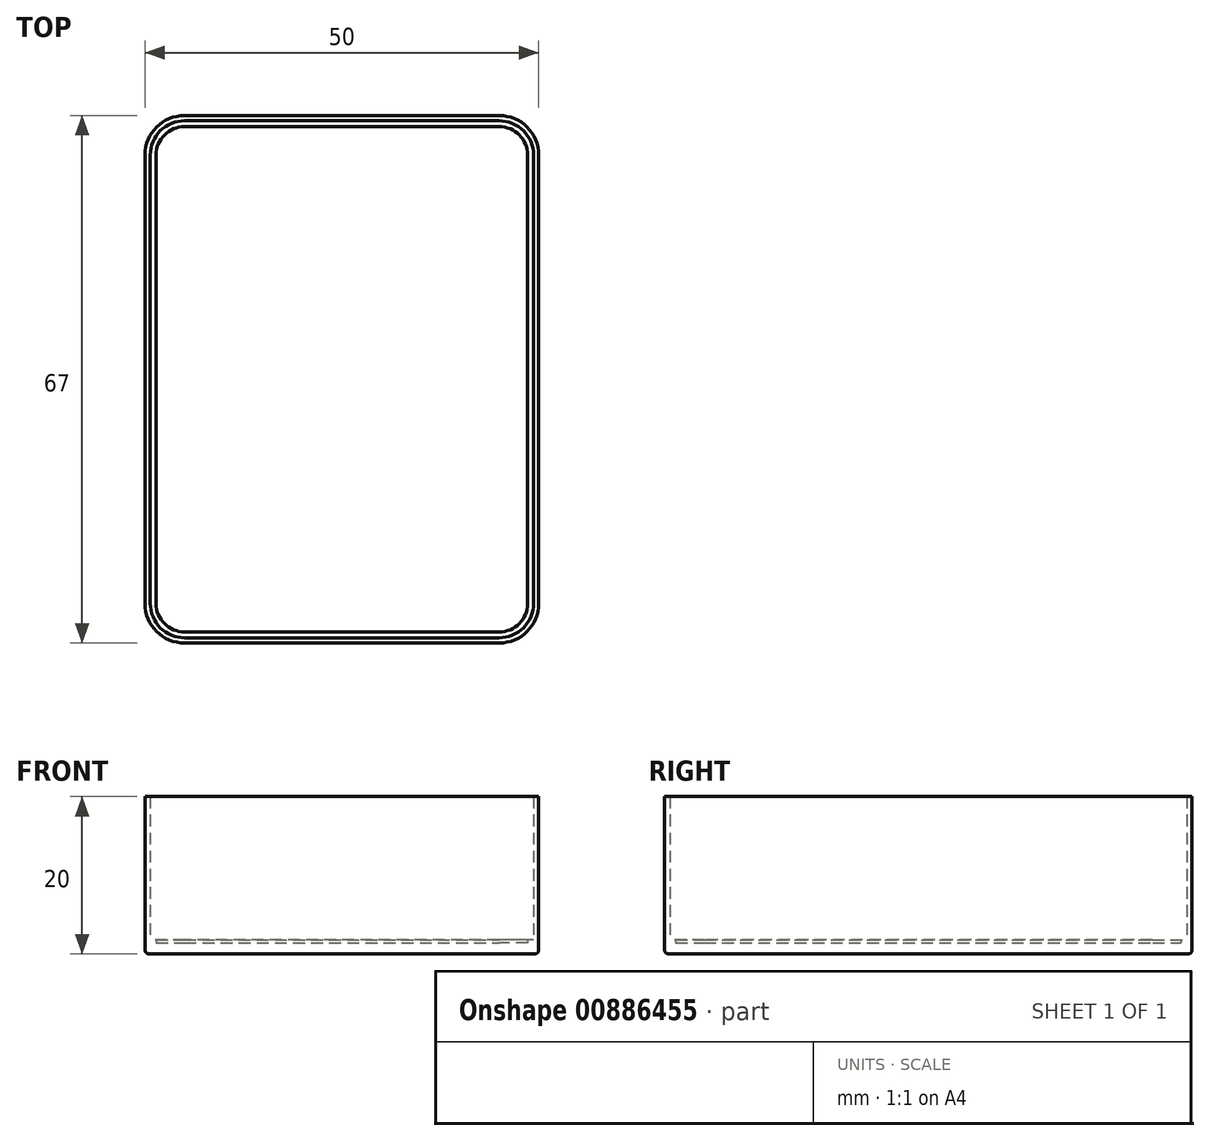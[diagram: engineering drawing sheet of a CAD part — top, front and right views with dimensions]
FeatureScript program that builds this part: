
annotation { "Feature Type Name" : "Feature", "Feature Type Description" : "" }
export const myFeature = defineFeature(function(context is Context, id is Id, definition is map)
    precondition{}
    {
        {
            assignVariable(context, id + "F0", {"name" : "Wandstaerke", "anyValue" : 1.4});
        }
        {
            assignVariable(context, id + "F1", {"name" : "Boxhoehe", "anyValue" : 20});
        }
        {
            assignVariable(context, id + "F2", {"name" : "Abrundungen", "anyValue" : 0.5});
        }
        {
            var Q0;
            Q0=qCreatedBy(makeId("Top.planeOp"),FACE);
            var sketch = newSketch(context, id + "F3", { "sketchPlane" : qUnion([Q0])});
            skLineSegment(sketch, "E0.bottom", {"start": v(-20, -33.5) * mm, "end": v(20, -33.5) * mm});
            skLineSegment(sketch, "E0.top", {"start": v(-20, 33.5) * mm, "end": v(20, 33.5) * mm});
            skLineSegment(sketch, "E0.left", {"start": v(-25, -28.5) * mm, "end": v(-25, 28.5) * mm});
            skLineSegment(sketch, "E0.right", {"start": v(25, -28.5) * mm, "end": v(25, 28.5) * mm});
            skPoint(sketch, "E0.middle", {"position": v(0, 0) * mm});
            skLineSegment(sketch, "E1.bottom", {"start": v(-20, -32.1) * mm, "end": v(20, -32.1) * mm});
            skLineSegment(sketch, "E1.top", {"start": v(-20, 32.1) * mm, "end": v(20, 32.1) * mm});
            skLineSegment(sketch, "E1.left", {"start": v(-23.6, -28.5) * mm, "end": v(-23.6, 28.5) * mm});
            skLineSegment(sketch, "E1.right", {"start": v(23.6, -28.5) * mm, "end": v(23.6, 28.5) * mm});
            skLineSegment(sketch, "E2.bottom", {"start": v(19.95, 32.85) * mm, "end": v(-19.95, 32.85) * mm});
            skLineSegment(sketch, "E2.top", {"start": v(19.95, -32.85) * mm, "end": v(-19.95, -32.85) * mm});
            skLineSegment(sketch, "E2.left", {"start": v(24.35, 28.45) * mm, "end": v(24.35, -28.45) * mm});
            skLineSegment(sketch, "E2.right", {"start": v(-24.35, 28.45) * mm, "end": v(-24.35, -28.45) * mm});
            skPoint(sketch, "E3.visualSharp", {"position": v(23.6, -32.1) * mm});
            skArc(sketch, "E3.filletArc", {"start": v(20, -32.1) * mm, "mid": v(22.55, -31.05) * mm, "end": v(23.6, -28.5) * mm});
            skPoint(sketch, "E4.visualSharp", {"position": v(24.35, -32.85) * mm});
            skArc(sketch, "E4.filletArc", {"start": v(19.95, -32.85) * mm, "mid": v(23.06, -31.56) * mm, "end": v(24.35, -28.45) * mm});
            skPoint(sketch, "E5.visualSharp", {"position": v(25, -33.5) * mm});
            skArc(sketch, "E5.filletArc", {"start": v(20, -33.5) * mm, "mid": v(23.54, -32.04) * mm, "end": v(25, -28.5) * mm});
            skPoint(sketch, "E6.visualSharp", {"position": v(23.6, 32.1) * mm});
            skArc(sketch, "E6.filletArc", {"start": v(23.6, 28.5) * mm, "mid": v(22.55, 31.05) * mm, "end": v(20, 32.1) * mm});
            skPoint(sketch, "E7.visualSharp", {"position": v(24.35, 32.85) * mm});
            skArc(sketch, "E7.filletArc", {"start": v(24.35, 28.45) * mm, "mid": v(23.06, 31.56) * mm, "end": v(19.95, 32.85) * mm});
            skPoint(sketch, "E8.visualSharp", {"position": v(25, 33.5) * mm});
            skArc(sketch, "E8.filletArc", {"start": v(25, 28.5) * mm, "mid": v(23.54, 32.04) * mm, "end": v(20, 33.5) * mm});
            skPoint(sketch, "E9.visualSharp", {"position": v(-23.6, 32.1) * mm});
            skArc(sketch, "E9.filletArc", {"start": v(-20, 32.1) * mm, "mid": v(-22.55, 31.05) * mm, "end": v(-23.6, 28.5) * mm});
            skPoint(sketch, "E10.visualSharp", {"position": v(-24.35, 32.85) * mm});
            skArc(sketch, "E10.filletArc", {"start": v(-19.95, 32.85) * mm, "mid": v(-23.06, 31.56) * mm, "end": v(-24.35, 28.45) * mm});
            skPoint(sketch, "E11.visualSharp", {"position": v(-25, 33.5) * mm});
            skArc(sketch, "E11.filletArc", {"start": v(-20, 33.5) * mm, "mid": v(-23.54, 32.04) * mm, "end": v(-25, 28.5) * mm});
            skPoint(sketch, "E12.visualSharp", {"position": v(-23.6, -32.1) * mm});
            skArc(sketch, "E12.filletArc", {"start": v(-23.6, -28.5) * mm, "mid": v(-22.55, -31.05) * mm, "end": v(-20, -32.1) * mm});
            skPoint(sketch, "E13.visualSharp", {"position": v(-24.35, -32.85) * mm});
            skArc(sketch, "E13.filletArc", {"start": v(-24.35, -28.45) * mm, "mid": v(-23.06, -31.56) * mm, "end": v(-19.95, -32.85) * mm});
            skPoint(sketch, "E14.visualSharp", {"position": v(-25, -33.5) * mm});
            skArc(sketch, "E14.filletArc", {"start": v(-25, -28.5) * mm, "mid": v(-23.54, -32.04) * mm, "end": v(-20, -33.5) * mm});
            skSolve(sketch);
        }
        {
            var Q0;
            Q0=makeQuery(id+"F3.imprint","IMPRINT",FACE,{"disambiguationData":[TD([[makeQuery(id+"F3.imprint","IMPRINT",EDGE,{"derivedFrom":sQuery(id+"F3.wireOp",EDGE,"E1.bottom")}),-1.0]])]});
            extrude(context, id + "F4", {"entities" : qUnion([Q0]), "depth" : (getVariable(context, 'Wandstaerke') + 0.4) * mm, "offsetDistance" : 25 * mm});
        }
        {
            var Q0;
            Q0=qSketchRegion(id+"F3",true);
            extrude(context, id + "F5", {"entities" : qUnion([Q0]), "operationType" : NewBodyOperationType.ADD, "depth" : (getVariable(context, 'Boxhoehe')) * mm, "offsetDistance" : 25 * mm});
        }
        {
            var Q0;
            Q0=makeQuery(id+"F3.imprint","IMPRINT",FACE,{"disambiguationData":[TD([[makeQuery(id+"F3.imprint","IMPRINT",EDGE,{"derivedFrom":sQuery(id+"F3.wireOp",EDGE,"E1.bottom")}),1.0]])]});
            extrude(context, id + "F6", {"entities" : qUnion([Q0]), "operationType" : NewBodyOperationType.ADD, "depth" : (getVariable(context, 'Wandstaerke')) * mm, "offsetDistance" : 25 * mm});
        }
        {
            var Q0;
            Q0=makeQuery(id+"F5.opExtrude","CAP_EDGE",EDGE,{"disambiguationData":[OSD([sQuery(id+"F3.wireOp",EDGE,"E0.right")])],"isStart":true});
            fillet(context, id + "F7", {"entities" : qUnion([Q0]), "radius" : (getVariable(context, 'Abrundungen')) * mm, "tangentPropagation" : true, "allowEdgeOverflow" : false});
        }
    });
